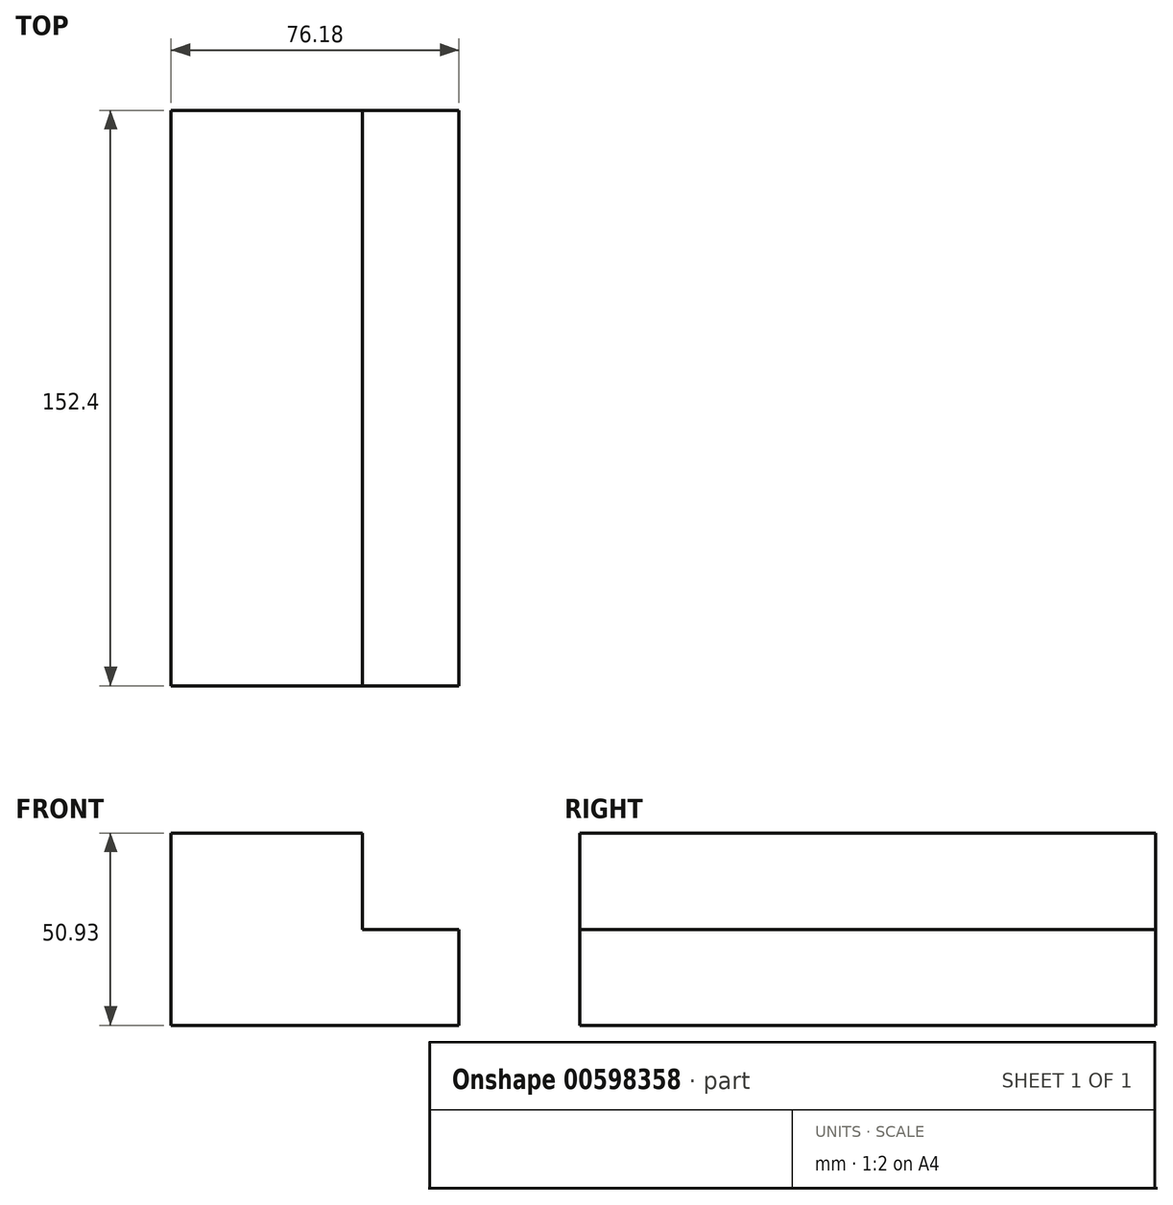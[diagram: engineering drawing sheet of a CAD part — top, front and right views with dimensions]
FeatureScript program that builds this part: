
annotation { "Feature Type Name" : "Feature", "Feature Type Description" : "" }
export const myFeature = defineFeature(function(context is Context, id is Id, definition is map)
    precondition{}
    {
        {
            var Q0;
            Q0=qCreatedBy(makeId("Front.planeOp"),FACE);
            var sketch = newSketch(context, id + "F0", { "sketchPlane" : qUnion([Q0])});
            skLineSegment(sketch, "E0", {"start": v(0, 0) * mm, "end": v(0, 50.93) * mm});
            skLineSegment(sketch, "E1", {"start": v(0, 50.93) * mm, "end": v(50.64, 50.93) * mm});
            skLineSegment(sketch, "E2", {"start": v(50.64, 50.93) * mm, "end": v(50.64, 25.4) * mm});
            skLineSegment(sketch, "E3", {"start": v(50.64, 25.4) * mm, "end": v(76.18, 25.4) * mm});
            skLineSegment(sketch, "E4", {"start": v(76.18, 25.4) * mm, "end": v(76.18, 0) * mm});
            skLineSegment(sketch, "E5", {"start": v(76.18, 0) * mm, "end": v(0, 0) * mm});
            skSolve(sketch);
        }
        {
            var Q0;
            Q0 = qSketchRegion(id + "F0", true);
            extrude(context, id + "F1", {"entities" : qUnion([Q0]), "depth" : 152.4 * mm, "offsetDistance" : 25.4 * mm});
        }
    });
